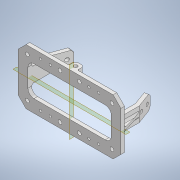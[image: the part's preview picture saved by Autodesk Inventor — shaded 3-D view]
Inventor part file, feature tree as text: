
AUTODESK INVENTOR PART (.ipt)
format: ipt  version: 2020 (Build 240168000, 168)  size: 561,152 bytes
history: native  units: mm
features: sketch x11, projected_geometry x11, other x11, extrude x9, thicken_offset x8, fillet x6, reference x6, mirror x5, chamfer x3, plane x2, hole x1
ambient origin geometry x8: Origin, YZ Plane, XZ Plane, XY Plane, X Axis, Y Axis, Z Axis, Center Point
bodies: Solid1 (feature_tree)
feature tree (73):
  extrude  "Extrusion1"  Depth=55.0mm
  extrude  "Extrusion2"  Depth=55.0mm
  thicken_offset  "Thicken1"
  thicken_offset  "Thicken2"
  thicken_offset  "Thicken3"
  thicken_offset  "Thicken4"
  plane  "Work Plane1"
  sketch  "Sketch3"  dims[d4=10.0mm d5=49.0mm]
  plane  "Work Plane2"
  extrude  "Extrusion3"  Depth=10.0mm
  extrude  "Extrusion4"  Depth=10.0mm
  mirror  "Mirror1"
  extrude  "Extrusion5"  Depth=3.0mm
  mirror  "Mirror2"
  extrude  "Extrusion6"  Depth=2.0mm
  mirror  "Mirror3"
  extrude  "Extrusion7"  Depth=2.0mm
  mirror  "Mirror4"
  extrude  "Extrusion8"  Depth=2.0mm
  mirror  "Mirror5"
  chamfer  "Chamfer2"  Distance=3.0mm
  fillet  "Fillet1"  Radius=5.0mm
  fillet  "Fillet2"  Radius=10.0mm
  chamfer  "Chamfer3"  Distance=5.0mm
  hole  "Hole1"  [1 undecoded]
  fillet  "Fillet3"  Radius=3.0mm
  fillet  "Fillet4"  Radius=3.0mm
  chamfer  "Chamfer4"  Distance=12.0mm
  thicken_offset  "Thicken5"
  thicken_offset  "Thicken6"
  thicken_offset  "Thicken7"
  thicken_offset  "Thicken8"
  fillet  "Fillet5"  Radius=2.0mm
  extrude  "Extrusion9"  Depth=3.0mm
  fillet  "Fillet6"  Radius=8.0mm
  sketch  "Sketch1"  dims[d0=12.0mm d1=55.0mm]
  reference  "Reference1"
  reference  "Reference2"
  reference  "Reference3"
  reference  "Reference4"
  sketch  "Sketch2"  dims[d2=12.0mm d3=55.0mm]
  projected_geometry  "Projected Loop1"
  sketch  "Sketch4"  dims[d6=10.0mm d7=49.0mm]
  reference  "Reference5"
  reference  "Reference6"
  projected_geometry  "Projected Loop2"
  sketch  "Sketch5"  dims[d8=3.0mm d9=0.0mm d10=2.0mm]
  projected_geometry  "Projected Loop3"
  projected_geometry  "Projected Loop4"
  sketch  "Sketch6"  dims[d11=2.0mm d12=2.0mm]
  projected_geometry  "Projected Loop5"
  projected_geometry  "Projected Loop6"
  sketch  "Sketch7"  dims[d13=2.0mm d14=2.0mm]
  projected_geometry  "Projected Loop7"
  sketch  "Sketch8"  dims[d15=2.0mm d16=2.0mm]
  projected_geometry  "Projected Loop8"
  sketch  "Sketch9"  dims[d17=2.0mm d18=3.0mm d19=0.0mm d20=5.0mm d21=10.0mm d22=7.0mm d23=10.0mm d24=5.0mm d25=7.0mm]
  projected_geometry  "Projected Loop9"
  sketch  "Sketch10"  dims[d26=7.0mm d27=7.0mm d28=3.0mm d29=3.0mm d30=12.0mm d31=0.0mm d32=2.0mm d33=0.0mm]
  projected_geometry  "Projected Loop10"
  sketch  "Sketch11"  dims[d34=2.0mm d35=0.0mm d36=4.0mm d37=8.0mm d38=3.1mm d39=3.1mm d40=2.0mm d41=0.0mm d45=8.0mm d46=8.0mm d47=3.1mm d48=3.1mm d49=10.0mm d50=0.0mm d51=2.0mm d52=7.0mm d53=7.0mm d54=3.1mm d55=5.0mm d56=0.0mm d57=1.5mm d58=2.0mm d59=45.0deg d60=2.0mm d61=5.0mm d62=8.0mm d63=2.0mm d64=45.0deg d65=33.0mm d66=70.0mm d67=3.1mm d68=6.0mm d69=4.0mm d70=2.0mm d71=90.0deg d72=20.0mm d73=0.0mm d74=2.0mm d75=1.5mm d76=2.0mm d77=2.0mm d78=45.0deg d79=1.5mm d80=1.5mm d81=1.5mm d82=1.5mm d83=1.5mm d84=1.5mm d85=1.5mm d86=1.5mm d87=1.0mm d88=6.0mm d89=25.0mm d90=10.0mm d91=0.0mm d92=3.0mm]
  projected_geometry  "Projected Loop11"
  parser-record x1  (decoder bookkeeping rows leaked as tree rows — omitted from the tree; the rows remain in map.json)
  other  "body_1.iam"
  other  "leg_1:1"
  other  "reducer_1:3"
  other  "mot_holder_1:1"
  other  "leg_1_MIR:1"
  other  "reducer_1_MIR:3"
  other  "mot_holder_1_MIR:1"
  other  "leg_1_MIR:2"
  other  "leg_1:2"
  other  "body_shell_2:1"
note: 1 required parameter value undecoded (feature->parameter linkage not recoverable at this tier; creation-order binding heuristic only, values carry confidence <= 0.55)
note: 1 file-system path scrubbed to <path> (originals preserved in map.json)
